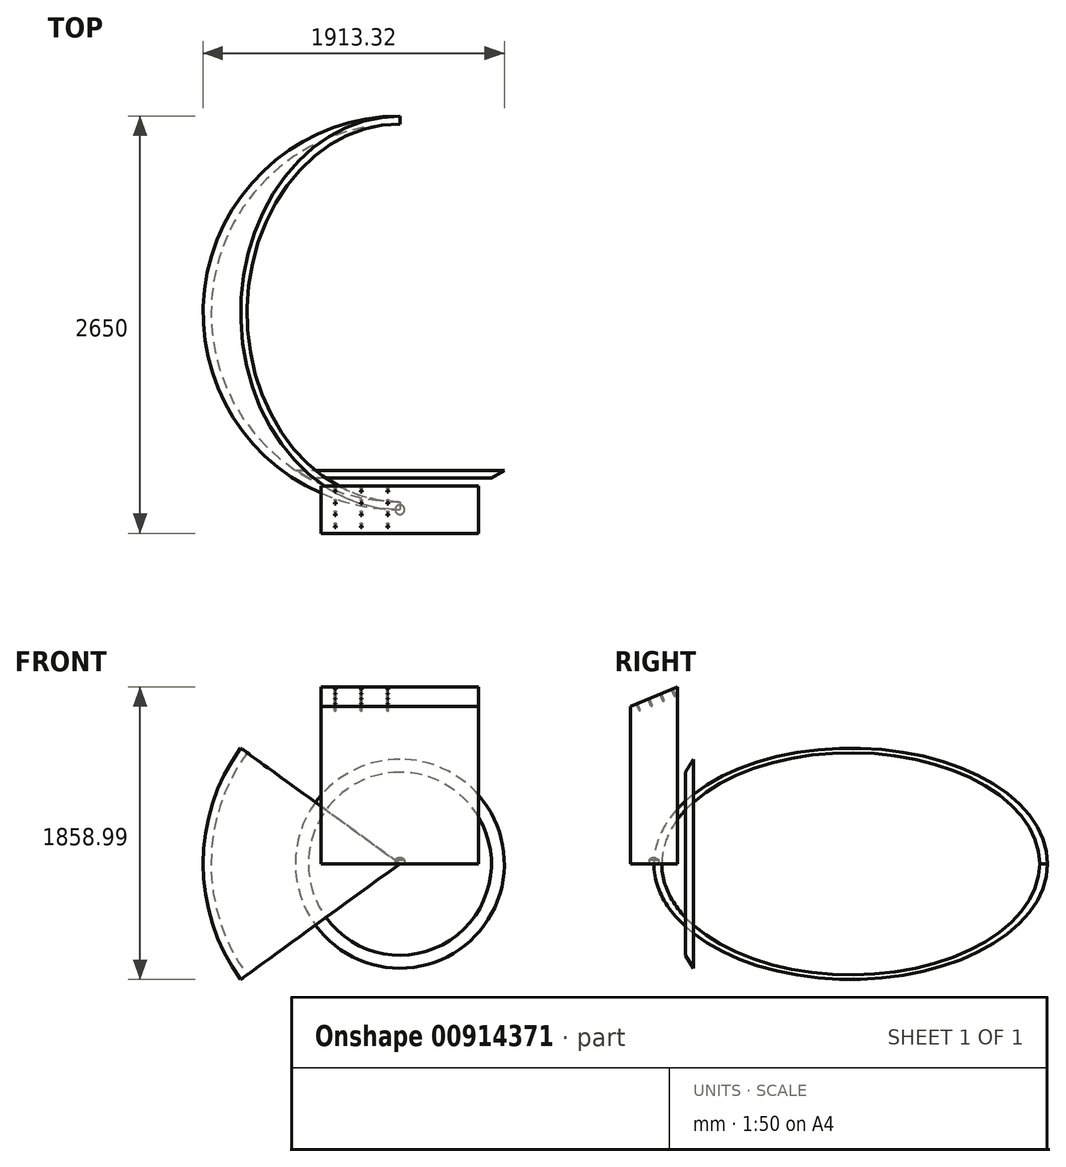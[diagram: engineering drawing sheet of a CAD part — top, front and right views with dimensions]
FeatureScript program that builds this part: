
annotation { "Feature Type Name" : "Feature", "Feature Type Description" : "" }
export const myFeature = defineFeature(function(context is Context, id is Id, definition is map)
    precondition{}
    {
        {
            var Q0;
            Q0=qCreatedBy(makeId("Right.planeOp"),FACE);
            var sketch = newSketch(context, id + "F0", { "sketchPlane" : qUnion([Q0])});
            skLineSegment(sketch, "E0", {"start": v(-150, 0) * mm, "end": v(150, 0) * mm});
            skLineSegment(sketch, "E1", {"start": v(150, 0) * mm, "end": v(150, 1124.26) * mm});
            skLineSegment(sketch, "E2", {"start": v(150, 1124.26) * mm, "end": v(-150, 1000) * mm});
            skLineSegment(sketch, "E3", {"start": v(-150, 1000) * mm, "end": v(-150, 0) * mm});
            skSolve(sketch);
        }
        {
            var Q0;
            Q0 = qSketchRegion(id + "F0", true);
            extrude(context, id + "F1", {"entities" : qUnion([Q0]), "endBound" : BoundingType.SYMMETRIC, "depth" : 1000 * mm, "offsetDistance" : 25 * mm});
        }
        {
            var Q0;
            Q0=qCreatedBy(makeId("Right.planeOp"),FACE);
            var sketch = newSketch(context, id + "F2", { "sketchPlane" : qUnion([Q0])});
            skLineSegment(sketch, "E4", {"start": v(-30, 0) * mm, "end": v(30, 0) * mm});
            skLineSegment(sketch, "E5", {"start": v(30, 0) * mm, "end": v(30, 25) * mm});
            skLineSegment(sketch, "E6", {"start": v(-30, 0) * mm, "end": v(-30, 25) * mm});
            skArc(sketch, "E7", {"start": v(30, 25) * mm, "mid": v(0, 37.5) * mm, "end": v(-30, 25) * mm});
            skLineSegment(sketch, "E8", {"start": v(-30, 25) * mm, "end": v(30, 25) * mm, "construction": true});
            skLineSegment(sketch, "E9", {"start": v(0, 0) * mm, "end": v(0, 37.5) * mm});
            skSolve(sketch);
        }
        {
            var Q0;
            {var subQ0=sQuery(id+"F2.wireOp",EDGE,"E6");Q0=makeQuery(id+"F2.imprint","IMPRINT",FACE,{"disambiguationData":[TD([[makeQuery(id+"F2.imprint","IMPRINT",EDGE,{"derivedFrom":subQ0}),-1.0]])]});}
            var Q1;
            Q1=sQuery(id+"F2.wireOp",EDGE,"E9");
            revolve(context, id + "F3", {"surfaceOperationType" : NewSurfaceOperationType.NEW, "entities" : qUnion([Q0]), "axis" : qUnion([Q1]), "revolveType" : RevolveType.FULL});
        }
        {
            var Q0;
            Q0=makeQuery(id+"F1.opExtrude","SWEPT_FACE",FACE,{"disambiguationData":[OSD([sQuery(id+"F0.wireOp",EDGE,"E2")])]});
            var sketch = newSketch(context, id + "F4", { "sketchPlane" : qUnion([Q0])});
            skLineSegment(sketch, "E10", {"start": v(-500, 365.87) * mm, "end": v(500, 365.87) * mm, "construction": true});
            skLineSegment(sketch, "E11", {"start": v(500, 365.87) * mm, "end": v(500, 447.05) * mm, "construction": true});
            skLineSegment(sketch, "E12", {"start": v(500, 447.05) * mm, "end": v(-500, 447.05) * mm, "construction": true});
            skLineSegment(sketch, "E13", {"start": v(500, 609.4) * mm, "end": v(-500, 609.4) * mm, "construction": true});
            skLineSegment(sketch, "E14", {"start": v(500, 365.87) * mm, "end": v(500, 284.7) * mm, "construction": true});
            skLineSegment(sketch, "E15", {"start": v(500, 284.7) * mm, "end": v(-500, 284.7) * mm, "construction": true});
            skLineSegment(sketch, "E16", {"start": v(500, 284.7) * mm, "end": v(500, 203.51) * mm, "construction": true});
            skLineSegment(sketch, "E17", {"start": v(500, 203.51) * mm, "end": v(-500, 203.51) * mm, "construction": true});
            skLineSegment(sketch, "E18", {"start": v(-500, 203.51) * mm, "end": v(0, 203.51) * mm, "construction": true});
            skLineSegment(sketch, "E19", {"start": v(-583.33, 203.51) * mm, "end": v(-416.67, 203.51) * mm, "construction": true});
            skLineSegment(sketch, "E20", {"start": v(-416.67, 203.51) * mm, "end": v(-250, 203.51) * mm, "construction": true});
            skLineSegment(sketch, "E21", {"start": v(-250, 203.51) * mm, "end": v(-83.33, 203.51) * mm, "construction": true});
            skLineSegment(sketch, "E22", {"start": v(-83.33, 203.51) * mm, "end": v(83.33, 203.51) * mm, "construction": true});
            skLineSegment(sketch, "E23", {"start": v(-416.67, 203.51) * mm, "end": v(-416.67, 609.4) * mm, "construction": true});
            skLineSegment(sketch, "E24", {"start": v(-250, 203.51) * mm, "end": v(-250, 609.4) * mm, "construction": true});
            skLineSegment(sketch, "E25", {"start": v(-83.33, 203.51) * mm, "end": v(-83.33, 609.4) * mm, "construction": true});
            skLineSegment(sketch, "E26.bottom", {"start": v(-416.67, 284.7) * mm, "end": v(-406.67, 284.7) * mm});
            skLineSegment(sketch, "E26.top", {"start": v(-416.67, 294.7) * mm, "end": v(-406.67, 294.7) * mm});
            skLineSegment(sketch, "E26.left", {"start": v(-416.67, 284.7) * mm, "end": v(-416.67, 294.7) * mm});
            skLineSegment(sketch, "E26.right", {"start": v(-406.67, 284.7) * mm, "end": v(-406.67, 294.7) * mm});
            skLineSegment(sketch, "E27.bottom", {"start": v(-416.67, 365.87) * mm, "end": v(-406.67, 365.87) * mm});
            skLineSegment(sketch, "E27.top", {"start": v(-416.67, 375.87) * mm, "end": v(-406.67, 375.87) * mm});
            skLineSegment(sketch, "E27.left", {"start": v(-416.67, 365.87) * mm, "end": v(-416.67, 375.87) * mm});
            skLineSegment(sketch, "E27.right", {"start": v(-406.67, 365.87) * mm, "end": v(-406.67, 375.87) * mm});
            skLineSegment(sketch, "E28.bottom", {"start": v(-416.67, 447.05) * mm, "end": v(-406.67, 447.05) * mm});
            skLineSegment(sketch, "E28.top", {"start": v(-416.67, 457.05) * mm, "end": v(-406.67, 457.05) * mm});
            skLineSegment(sketch, "E28.left", {"start": v(-416.67, 447.05) * mm, "end": v(-416.67, 457.05) * mm});
            skLineSegment(sketch, "E28.right", {"start": v(-406.67, 447.05) * mm, "end": v(-406.67, 457.05) * mm});
            skLineSegment(sketch, "E29.bottom", {"start": v(-250, 284.7) * mm, "end": v(-240, 284.7) * mm});
            skLineSegment(sketch, "E29.top", {"start": v(-250, 294.7) * mm, "end": v(-240, 294.7) * mm});
            skLineSegment(sketch, "E29.left", {"start": v(-250, 284.7) * mm, "end": v(-250, 294.7) * mm});
            skLineSegment(sketch, "E29.right", {"start": v(-240, 284.7) * mm, "end": v(-240, 294.7) * mm});
            skLineSegment(sketch, "E30.bottom", {"start": v(-250, 365.87) * mm, "end": v(-240, 365.87) * mm});
            skLineSegment(sketch, "E30.top", {"start": v(-250, 375.87) * mm, "end": v(-240, 375.87) * mm});
            skLineSegment(sketch, "E30.left", {"start": v(-250, 365.87) * mm, "end": v(-250, 375.87) * mm});
            skLineSegment(sketch, "E30.right", {"start": v(-240, 365.87) * mm, "end": v(-240, 375.87) * mm});
            skLineSegment(sketch, "E31.bottom", {"start": v(-250, 447.05) * mm, "end": v(-240, 447.05) * mm});
            skLineSegment(sketch, "E31.top", {"start": v(-250, 457.05) * mm, "end": v(-240, 457.05) * mm});
            skLineSegment(sketch, "E31.left", {"start": v(-250, 447.05) * mm, "end": v(-250, 457.05) * mm});
            skLineSegment(sketch, "E31.right", {"start": v(-240, 447.05) * mm, "end": v(-240, 457.05) * mm});
            skLineSegment(sketch, "E32.bottom", {"start": v(-83.33, 284.7) * mm, "end": v(-73.33, 284.7) * mm});
            skLineSegment(sketch, "E32.top", {"start": v(-83.33, 294.7) * mm, "end": v(-73.33, 294.7) * mm});
            skLineSegment(sketch, "E32.left", {"start": v(-83.33, 284.7) * mm, "end": v(-83.33, 294.7) * mm});
            skLineSegment(sketch, "E32.right", {"start": v(-73.33, 284.7) * mm, "end": v(-73.33, 294.7) * mm});
            skLineSegment(sketch, "E33.bottom", {"start": v(-83.33, 365.87) * mm, "end": v(-73.33, 365.87) * mm});
            skLineSegment(sketch, "E33.top", {"start": v(-83.33, 375.87) * mm, "end": v(-73.33, 375.87) * mm});
            skLineSegment(sketch, "E33.left", {"start": v(-83.33, 365.87) * mm, "end": v(-83.33, 375.87) * mm});
            skLineSegment(sketch, "E33.right", {"start": v(-73.33, 365.87) * mm, "end": v(-73.33, 375.87) * mm});
            skLineSegment(sketch, "E34.bottom", {"start": v(-83.33, 447.05) * mm, "end": v(-73.33, 447.05) * mm});
            skLineSegment(sketch, "E34.top", {"start": v(-83.33, 457.05) * mm, "end": v(-73.33, 457.05) * mm});
            skLineSegment(sketch, "E34.left", {"start": v(-83.33, 447.05) * mm, "end": v(-83.33, 457.05) * mm});
            skLineSegment(sketch, "E34.right", {"start": v(-73.33, 447.05) * mm, "end": v(-73.33, 457.05) * mm});
            skLineSegment(sketch, "E35", {"start": v(500, 528.23) * mm, "end": v(-500, 528.23) * mm, "construction": true});
            skLineSegment(sketch, "E36", {"start": v(500, 528.23) * mm, "end": v(500, 447.05) * mm, "construction": true});
            skLineSegment(sketch, "E37", {"start": v(500, 528.23) * mm, "end": v(500, 609.4) * mm, "construction": true});
            skCircle(sketch, "E38", {"center": v(-416.67, 284.7) * mm, "radius": 30 * mm, "construction": true});
            skCircle(sketch, "E39", {"center": v(-416.67, 365.87) * mm, "radius": 30 * mm, "construction": true});
            skCircle(sketch, "E40", {"center": v(-416.67, 447.05) * mm, "radius": 30 * mm, "construction": true});
            skCircle(sketch, "E41", {"center": v(-250, 284.7) * mm, "radius": 30 * mm, "construction": true});
            skCircle(sketch, "E42", {"center": v(-250, 365.87) * mm, "radius": 30 * mm, "construction": true});
            skCircle(sketch, "E43", {"center": v(-250, 447.05) * mm, "radius": 30 * mm, "construction": true});
            skCircle(sketch, "E44", {"center": v(-83.33, 284.7) * mm, "radius": 30 * mm, "construction": true});
            skCircle(sketch, "E45", {"center": v(-83.33, 365.87) * mm, "radius": 30 * mm, "construction": true});
            skCircle(sketch, "E46", {"center": v(-83.33, 447.05) * mm, "radius": 30 * mm, "construction": true});
            skLineSegment(sketch, "E47.bottom", {"start": v(-416.67, 528.23) * mm, "end": v(-406.67, 528.23) * mm});
            skLineSegment(sketch, "E47.top", {"start": v(-416.67, 538.23) * mm, "end": v(-406.67, 538.23) * mm});
            skLineSegment(sketch, "E47.left", {"start": v(-416.67, 528.23) * mm, "end": v(-416.67, 538.23) * mm});
            skLineSegment(sketch, "E47.right", {"start": v(-406.67, 528.23) * mm, "end": v(-406.67, 538.23) * mm});
            skLineSegment(sketch, "E48.bottom", {"start": v(-250, 528.23) * mm, "end": v(-240, 528.23) * mm});
            skLineSegment(sketch, "E48.top", {"start": v(-250, 538.23) * mm, "end": v(-240, 538.23) * mm});
            skLineSegment(sketch, "E48.left", {"start": v(-250, 528.23) * mm, "end": v(-250, 538.23) * mm});
            skLineSegment(sketch, "E48.right", {"start": v(-240, 528.23) * mm, "end": v(-240, 538.23) * mm});
            skLineSegment(sketch, "E49.bottom", {"start": v(-83.33, 528.23) * mm, "end": v(-73.33, 528.23) * mm});
            skLineSegment(sketch, "E49.top", {"start": v(-83.33, 538.23) * mm, "end": v(-73.33, 538.23) * mm});
            skLineSegment(sketch, "E49.left", {"start": v(-83.33, 528.23) * mm, "end": v(-83.33, 538.23) * mm});
            skLineSegment(sketch, "E49.right", {"start": v(-73.33, 528.23) * mm, "end": v(-73.33, 538.23) * mm});
            skSolve(sketch);
        }
        {
            var Q0;
            Q0 = qSketchRegion(id + "F4", true);
            extrude(context, id + "F5", {"entities" : qUnion([Q0]), "operationType" : NewBodyOperationType.REMOVE, "oppositeDirection" : true, "depth" : 50 * mm, "offsetDistance" : 25 * mm});
        }
        {
            var Q0;
            Q0=qCreatedBy(makeId("Top.planeOp"),FACE);
            var sketch = newSketch(context, id + "F6", { "sketchPlane" : qUnion([Q0])});
            skLineSegment(sketch, "E50", {"start": v(0, 2450) * mm, "end": v(0, 50) * mm, "construction": true});
            skArc(sketch, "E51", {"start": v(0, 2450) * mm, "mid": v(-1200, 1250) * mm, "end": v(0, 50) * mm});
            skLineSegment(sketch, "E52", {"start": v(0, 2450) * mm, "end": v(0, 2500) * mm});
            skLineSegment(sketch, "E53", {"start": v(0, 50) * mm, "end": v(0, 0) * mm});
            skArc(sketch, "E54", {"start": v(0, 2500) * mm, "mid": v(-1250, 1250) * mm, "end": v(0, 0) * mm});
            skLineSegment(sketch, "E55", {"start": v(0, 250) * mm, "end": v(-663.32, 250) * mm});
            skLineSegment(sketch, "E56", {"start": v(0, 200) * mm, "end": v(-580.95, 200) * mm});
            skLineSegment(sketch, "E57", {"start": v(0, 200) * mm, "end": v(0, 250) * mm});
            skLineSegment(sketch, "E58", {"start": v(-580.95, 200) * mm, "end": v(-663.32, 250) * mm});
            skLineSegment(sketch, "E59", {"start": v(0, 250) * mm, "end": v(-750, 250) * mm, "construction": true});
            skSolve(sketch);
        }
        {
            var Q0;
            {var subQ1=sQuery(id+"F6.wireOp",EDGE,"E52");Q0=makeQuery(id+"F6.imprint","IMPRINT",FACE,{"disambiguationData":[TD([[makeQuery(id+"F6.imprint","IMPRINT",EDGE,{"derivedFrom":subQ1}),1.0]])]});}
            var Q1;
            Q1=sQuery(id+"F6.wireOp",EDGE,"E50");
            revolve(context, id + "F7", {"surfaceOperationType" : NewSurfaceOperationType.NEW, "entities" : qUnion([Q0]), "axis" : qUnion([Q1]), "revolveType" : RevolveType.SYMMETRIC, "angle" : 72 * degree});
        }
        {
            var Q0;
            Q0=makeQuery(id+"F6.imprint","IMPRINT",FACE,{"disambiguationData":[TD([[makeQuery(id+"F6.imprint","IMPRINT",EDGE,{"derivedFrom":sQuery(id+"F6.wireOp",EDGE,"E55")}),1.0]])]});
            var Q1;
            Q1=sQuery(id+"F6.wireOp",EDGE,"E50");
            revolve(context, id + "F8", {"surfaceOperationType" : NewSurfaceOperationType.NEW, "entities" : qUnion([Q0]), "axis" : qUnion([Q1]), "revolveType" : RevolveType.FULL});
        }
    });
